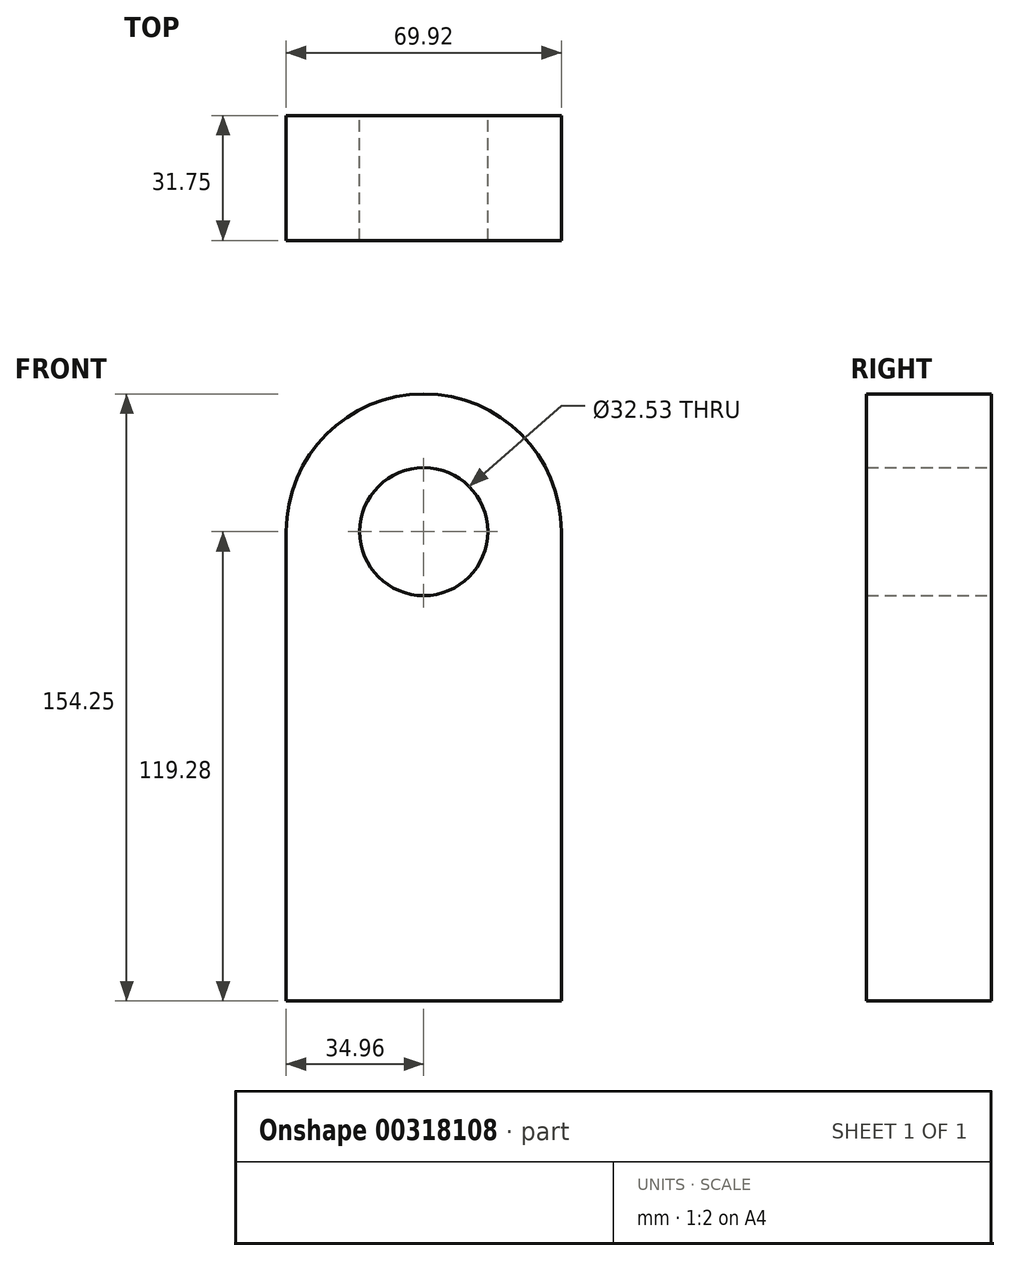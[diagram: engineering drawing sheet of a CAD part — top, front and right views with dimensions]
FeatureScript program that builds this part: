
annotation { "Feature Type Name" : "Feature", "Feature Type Description" : "" }
export const myFeature = defineFeature(function(context is Context, id is Id, definition is map)
    precondition{}
    {
        {
            var Q0;
            Q0=qCreatedBy(makeId("Front.planeOp"),FACE);
            var sketch = newSketch(context, id + "F0", { "sketchPlane" : qUnion([Q0])});
            skLineSegment(sketch, "E0.top", {"start": v(-34.96, -59.64) * mm, "end": v(34.96, -59.64) * mm});
            skLineSegment(sketch, "E0.left", {"start": v(-34.96, 59.64) * mm, "end": v(-34.96, -59.64) * mm});
            skLineSegment(sketch, "E0.right", {"start": v(34.96, 59.64) * mm, "end": v(34.96, -59.64) * mm});
            skPoint(sketch, "E0.middle", {"position": v(0, 0) * mm});
            skArc(sketch, "E1", {"start": v(34.96, 59.64) * mm, "mid": v(0, 94.6) * mm, "end": v(-34.96, 59.64) * mm});
            skCircle(sketch, "E2", {"center": v(0, 59.64) * mm, "radius": 16.26 * mm});
            skSolve(sketch);
        }
        {
            var Q0;
            Q0=makeQuery(id+"F0.imprint","IMPRINT",FACE,{"disambiguationData":[TD([[makeQuery(id+"F0.imprint","IMPRINT",EDGE,{"derivedFrom":sQuery(id+"F0.wireOp",EDGE,"E0.top")}),1.0]])]});
            extrude(context, id + "F1", {"entities" : qUnion([Q0]), "depth" : 31.75 * mm});
        }
    });
